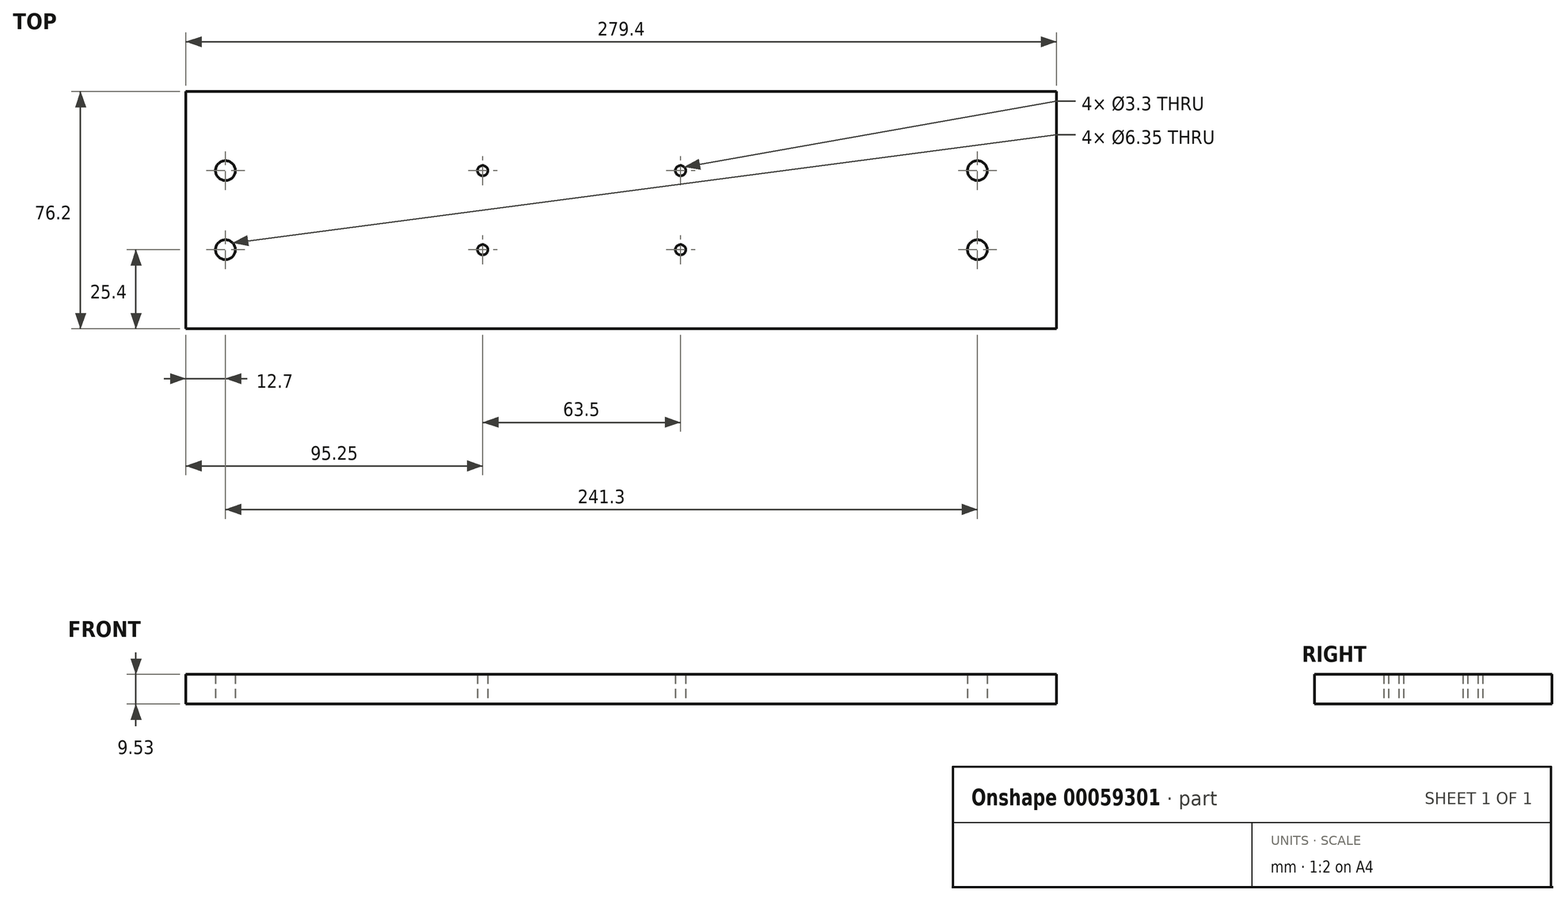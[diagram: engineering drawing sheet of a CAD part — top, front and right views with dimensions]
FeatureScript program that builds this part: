
annotation { "Feature Type Name" : "Feature", "Feature Type Description" : "" }
export const myFeature = defineFeature(function(context is Context, id is Id, definition is map)
    precondition{}
    {
        {
            var Q0;
            Q0=qCreatedBy(makeId("Top.planeOp"),FACE);
            var sketch = newSketch(context, id + "F0", { "sketchPlane" : qUnion([Q0])});
            skLineSegment(sketch, "E0.bottom", {"start": v(0, 0) * mm, "end": v(279.4, 0) * mm});
            skLineSegment(sketch, "E0.top", {"start": v(0, 76.2) * mm, "end": v(279.4, 76.2) * mm});
            skLineSegment(sketch, "E0.left", {"start": v(0, 0) * mm, "end": v(0, 76.2) * mm});
            skLineSegment(sketch, "E0.right", {"start": v(279.4, 0) * mm, "end": v(279.4, 76.2) * mm});
            skCircle(sketch, "E1", {"center": v(12.7, 50.8) * mm, "radius": 3.18 * mm});
            skCircle(sketch, "E2", {"center": v(95.25, 50.8) * mm, "radius": 1.65 * mm});
            skCircle(sketch, "E3", {"center": v(158.75, 50.8) * mm, "radius": 1.65 * mm});
            skCircle(sketch, "E4", {"center": v(254, 50.8) * mm, "radius": 3.18 * mm});
            skCircle(sketch, "E5", {"center": v(254, 25.4) * mm, "radius": 3.18 * mm});
            skCircle(sketch, "E6", {"center": v(158.75, 25.4) * mm, "radius": 1.65 * mm});
            skCircle(sketch, "E7", {"center": v(95.25, 25.4) * mm, "radius": 1.65 * mm});
            skCircle(sketch, "E8", {"center": v(12.7, 25.4) * mm, "radius": 3.18 * mm});
            skSolve(sketch);
        }
        {
            var Q0;
            Q0=makeQuery(id+"F0.imprint","IMPRINT",FACE,{"disambiguationData":[TD([[makeQuery(id+"F0.imprint","IMPRINT",EDGE,{"derivedFrom":sQuery(id+"F0.wireOp",EDGE,"E0.bottom")}),1.0]])]});
            extrude(context, id + "F1", {"entities" : qUnion([Q0]), "depth" : 9.52 * mm});
        }
    });
